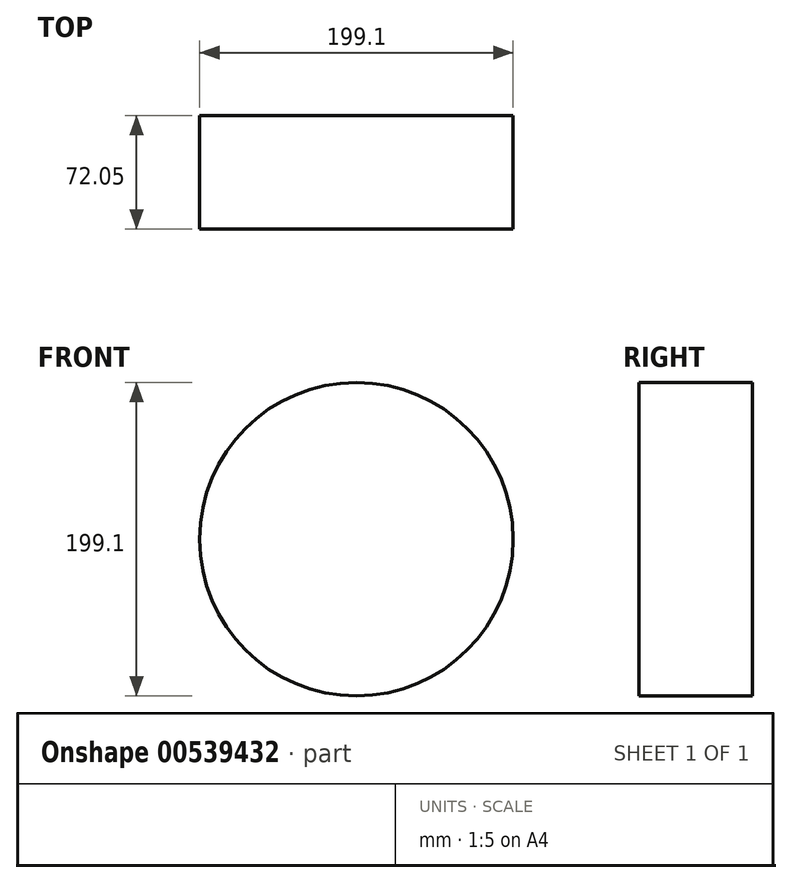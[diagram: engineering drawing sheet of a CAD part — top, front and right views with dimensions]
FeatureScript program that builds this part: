
annotation { "Feature Type Name" : "Feature", "Feature Type Description" : "" }
export const myFeature = defineFeature(function(context is Context, id is Id, definition is map)
    precondition{}
    {
        {
            var Q0;
            Q0=qCreatedBy(makeId("Front.planeOp"),FACE);
            var sketch = newSketch(context, id + "F0", { "sketchPlane" : qUnion([Q0])});
            skCircle(sketch, "E0", {"center": v(0, 0) * mm, "radius": 99.55 * mm});
            skSolve(sketch);
        }
        {
            var Q0;
            Q0 = qSketchRegion(id + "F0", true);
            extrude(context, id + "F1", {"entities" : qUnion([Q0]), "depth" : 72.05 * mm, "offsetDistance" : 25.4 * mm});
        }
    });
